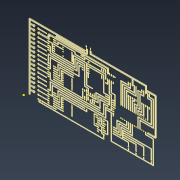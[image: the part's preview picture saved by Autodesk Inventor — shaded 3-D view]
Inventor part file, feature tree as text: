
AUTODESK INVENTOR PART (.ipt)
format: ipt  version: 2022.3 (Build 263350000, 350)  size: 3,169,280 bytes
history: mixed  units: in
note: dims shown in document units (in); Inventor stores cm internally (conversion verified against a paired STEP export)
features: other x156, projected_geometry x6, sketch x2, extrude x1, imported_body x1
ambient origin geometry x8: Origin, YZ Plane, XZ Plane, XY Plane, X Axis, Y Axis, Z Axis, Center Point
bodies: Solid1 (imported_parasolid), Solid2 (imported_parasolid), Solid3 (imported_parasolid), Solid4 (imported_parasolid), Solid5 (imported_parasolid), Solid6 (imported_parasolid), Solid7 (imported_parasolid), Solid8 (imported_parasolid), Solid9 (imported_parasolid), Solid10 (imported_parasolid), Solid11 (imported_parasolid), Solid12 (imported_parasolid), Solid13 (imported_parasolid), Solid14 (imported_parasolid), Solid15 (imported_parasolid), Solid16 (imported_parasolid), Solid17 (imported_parasolid), Solid18 (imported_parasolid), Solid19 (imported_parasolid), Solid20 (imported_parasolid), Solid21 (imported_parasolid), Solid22 (imported_parasolid), Solid23 (imported_parasolid), Solid24 (imported_parasolid), Solid25 (imported_parasolid), Solid26 (imported_parasolid), Solid27 (imported_parasolid), Solid28 (imported_parasolid), Solid29 (imported_parasolid), Solid30 (imported_parasolid), Solid31 (imported_parasolid), Solid32 (imported_parasolid), Solid33 (imported_parasolid), Solid34 (imported_parasolid), Solid35 (imported_parasolid), Solid36 (imported_parasolid), Solid37 (imported_parasolid), Solid38 (imported_parasolid), Solid39 (imported_parasolid), Solid40 (imported_parasolid), Solid41 (imported_parasolid), Solid42 (imported_parasolid), Solid43 (imported_parasolid), Solid44 (imported_parasolid), Solid45 (imported_parasolid), Solid46 (imported_parasolid), Solid47 (imported_parasolid), Solid48 (imported_parasolid), Solid49 (imported_parasolid), Solid50 (imported_parasolid), Solid51 (imported_parasolid), Solid52 (imported_parasolid), Solid53 (imported_parasolid), Solid54 (imported_parasolid), Solid55 (imported_parasolid), Solid56 (imported_parasolid), Solid57 (imported_parasolid), Solid58 (imported_parasolid), Solid59 (imported_parasolid), Solid60 (imported_parasolid), Solid61 (imported_parasolid), Solid62 (imported_parasolid), Solid63 (imported_parasolid), Solid64 (imported_parasolid), Solid65 (imported_parasolid), Solid66 (imported_parasolid), Solid67 (imported_parasolid), Solid68 (imported_parasolid), Solid69 (imported_parasolid), Solid70 (imported_parasolid), Solid71 (imported_parasolid), Solid72 (imported_parasolid), Solid73 (imported_parasolid), Solid74 (imported_parasolid), Solid75 (imported_parasolid), Solid76 (imported_parasolid), Solid77 (imported_parasolid), Solid78 (imported_parasolid), Solid79 (imported_parasolid), Solid80 (imported_parasolid), Solid81 (imported_parasolid), Solid82 (imported_parasolid), Solid83 (imported_parasolid), Solid84 (imported_parasolid), Solid85 (imported_parasolid), Solid92 (imported_parasolid), Solid93 (imported_parasolid), Solid102 (imported_parasolid), Solid103 (imported_parasolid), Solid104 (imported_parasolid), Solid113 (imported_parasolid), Solid114 (imported_parasolid), Solid117 (imported_parasolid), Solid118 (imported_parasolid), Solid119 (imported_parasolid), Solid120 (imported_parasolid), Solid121 (imported_parasolid), Solid122 (imported_parasolid), Solid123 (imported_parasolid), Solid124 (imported_parasolid), Solid125 (imported_parasolid), Solid126 (imported_parasolid), Solid127 (imported_parasolid), Solid128 (imported_parasolid), Solid129 (imported_parasolid), Solid130 (imported_parasolid), Solid131 (imported_parasolid), Solid132 (imported_parasolid), Solid133 (imported_parasolid), Solid134 (imported_parasolid), Solid135 (imported_parasolid), Solid136 (imported_parasolid), Solid137 (imported_parasolid), Solid138 (imported_parasolid), Solid139 (imported_parasolid), Solid140 (imported_parasolid), Solid141 (imported_parasolid), Solid142 (imported_parasolid), Solid143 (imported_parasolid), Solid144 (imported_parasolid), Solid145 (imported_parasolid), Solid146 (imported_parasolid), Solid147 (imported_parasolid), Solid148 (imported_parasolid), Solid149 (imported_parasolid), Solid150 (imported_parasolid), Solid151 (imported_parasolid), Solid152 (imported_parasolid), Solid153 (imported_parasolid), Solid154 (imported_parasolid), Solid155 (imported_parasolid), Solid156 (imported_parasolid), Solid157 (imported_parasolid), Solid158 (imported_parasolid), Solid159 (imported_parasolid), Solid160 (imported_parasolid), Solid161 (imported_parasolid), Solid162 (imported_parasolid), Solid163 (imported_parasolid), Solid164 (imported_parasolid), Solid165 (imported_parasolid), Solid166 (imported_parasolid), Solid167 (imported_parasolid), Solid168 (imported_parasolid), Solid169 (imported_parasolid), Solid170 (imported_parasolid), Solid171 (imported_parasolid), Solid172 (imported_parasolid), Solid173 (imported_parasolid), Solid174 (imported_parasolid), Solid175 (imported_parasolid), Solid176 (imported_parasolid), Solid177 (imported_parasolid), Solid178 (imported_parasolid), Solid179 (imported_parasolid), Solid180 (imported_parasolid), Solid181 (imported_parasolid), Body1 (imported_parasolid)
feature tree (166):
  sketch  "Sketch1"  dims[d0=0.0394in d1=0.0in]
  extrude  "Extrusion1"  [1 undecoded]
  sketch  "Sketch2"
  projected_geometry  "Projected Loop1"
  projected_geometry  "Projected Loop2"
  projected_geometry  "Projected Loop3"
  projected_geometry  "Projected Loop4"
  projected_geometry  "Projected Loop5"
  projected_geometry  "Projected Loop6"
  other  "Body1:1"
  other  "Body1:2"
  other  "Body1:3"
  other  "Body1:4"
  other  "Body1:5"
  other  "Body1:6"
  other  "Body1:7"
  other  "Body1:8"
  other  "Body1:9"
  other  "Body1:10"
  other  "Body1:11"
  other  "Body1:12"
  other  "Body1:13"
  other  "Body1:14"
  other  "Body1:15"
  other  "Body1:16"
  other  "Body1:17"
  other  "Body1:18"
  other  "Body1:19"
  other  "Body1:20"
  other  "Body1:21"
  other  "Body1:22"
  other  "Body1:23"
  other  "Body1:24"
  other  "Body1:25"
  other  "Body1:26"
  other  "Body1:27"
  other  "Body1:28"
  other  "Body1:29"
  other  "Body1:30"
  other  "Body1:31"
  other  "Body1:32"
  other  "Body1:33"
  other  "Body1:34"
  other  "Body1:35"
  other  "Body1:36"
  other  "Body1:37"
  other  "Body1:38"
  other  "Body1:39"
  other  "Body1:40"
  other  "Body1:41"
  other  "Body1:42"
  other  "Body1:43"
  other  "Body1:44"
  other  "Body1:45"
  other  "Body1:46"
  other  "Body1:47"
  other  "Body1:48"
  other  "Body1:49"
  other  "Body1:50"
  other  "Body1:51"
  other  "Body1:52"
  other  "Body1:53"
  other  "Body1:54"
  other  "Body1:55"
  other  "Body1:56"
  other  "Body1:57"
  other  "Body1:58"
  other  "Body1:59"
  other  "Body1:60"
  other  "Body1:61"
  other  "Body1:62"
  other  "Body1:63"
  other  "Body1:64"
  other  "Body1:65"
  other  "Body1:66"
  other  "Body1:67"
  other  "Body1:68"
  other  "Body1:69"
  other  "Body1:70"
  other  "Body1:71"
  other  "Body1:72"
  other  "Body1:73"
  other  "Body1:74"
  other  "Body1:75"
  other  "Body1:76"
  other  "Body1:77"
  other  "Body1:78"
  other  "Body1:79"
  other  "Body1:80"
  other  "Body1:81"
  other  "Body1:82"
  other  "Body1:83"
  other  "Body1:84"
  other  "Body1:91"
  other  "Body1:92"
  other  "Body1:101"
  other  "Body1:102"
  other  "Body1:103"
  other  "Body1:112"
  other  "Body1:113"
  other  "Body1:116"
  other  "Body1:117"
  other  "Body1:118"
  other  "Body1:119"
  other  "Body1:120"
  other  "Body1:121"
  other  "Body1:122"
  other  "Body1:123"
  other  "Body1:124"
  other  "Body1:125"
  other  "Body1:126"
  other  "Body1:127"
  other  "Body1:128"
  other  "Body1:129"
  other  "Body1:130"
  other  "Body1:131"
  other  "Body1:132"
  other  "Body1:133"
  other  "Body1:134"
  other  "Body1:135"
  other  "Body1:136"
  other  "Body1:137"
  other  "Body1:138"
  other  "Body1:139"
  other  "Body1:140"
  other  "Body1:141"
  other  "Body1:142"
  other  "Body1:143"
  other  "Body1:144"
  other  "Body1:145"
  other  "Body1:146"
  other  "Body1:147"
  other  "Body1:148"
  other  "Body1:149"
  other  "Body1:150"
  other  "Body1:151"
  other  "Body1:152"
  other  "Body1:153"
  other  "Body1:154"
  other  "Body1:155"
  other  "Body1:156"
  other  "Body1:157"
  other  "Body1:158"
  other  "Body1:159"
  other  "Body1:160"
  other  "Body1:161"
  other  "Body1:162"
  other  "Body1:163"
  other  "Body1:164"
  other  "Body1:165"
  other  "Body1:166"
  other  "Body1:167"
  other  "Body1:168"
  other  "Body1:169"
  other  "Body1:170"
  other  "Body1:171"
  other  "Body1:172"
  other  "Body1:173"
  other  "Body1:174"
  other  "Body1:175"
  other  "Body1:176"
  other  "Body1:177"
  other  "Body1:178"
  other  "Body1:179"
  other  "Body1:180"
  imported_body  NMx_Import_Brep_tag  [imported B-rep: ~2600 faces, bbox_mm=[168.945522, 96.522919, 1.0]]
note: 1 required parameter value undecoded (feature->parameter linkage not recoverable at this tier; creation-order binding heuristic only, values carry confidence <= 0.55)
